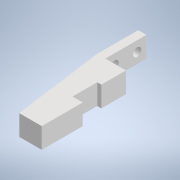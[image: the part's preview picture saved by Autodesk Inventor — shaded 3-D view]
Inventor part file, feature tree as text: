
AUTODESK INVENTOR PART (.ipt)
format: ipt  version: 2021 (Build 250183000, 183)  size: 149,504 bytes
history: native  units: mm
features: move_body x5, direct_edit x4, other x4, extrude x3, sketch x3, reference x2, fillet x1
ambient origin geometry x8: Origin, YZ Plane, XZ Plane, XY Plane, X Axis, Y Axis, Z Axis, Center Point
bodies: Solid1 (feature_tree)
feature tree (22):
  extrude  "Extrusion1"  Depth=20.0mm
  extrude  "Extrusion2"  Depth=12.0mm
  direct_edit  "Direct Edit1"
  direct_edit  "Direct Edit2"
  direct_edit  "Direct Edit3"
  extrude  "Extrusion3"  Depth=12.0mm
  direct_edit  "Direct Edit4"
  fillet  "Fillet1"  Radius=10.0mm
  sketch  "Sketch1"  dims[d0=4.0mm d1=20.0mm]
  sketch  "Sketch2"  dims[d2=14.0mm d3=12.0mm]
  reference  "Reference1"
  reference  "Reference2"
  sketch  "Sketch3"  dims[d4=12.0mm d5=12.0mm d6=10.0mm d7=20.0mm d8=10.0mm d9=0.0mm d10=10.0mm d11=0.0mm d12=0.0mm d13=0.0mm d14=7.0mm d15=0.0mm d16=0.0mm d17=2.0mm d18=0.0mm d19=0.0mm d20=8.0mm d21=0.0mm d22=0.0mm d23=7.75mm d24=10.0mm d25=0.0mm d26=0.0mm d27=0.0mm d28=0.5mm d29=2.0mm]
  parser-record x1  (decoder bookkeeping rows leaked as tree rows — omitted from the tree; the rows remain in map.json)
  other  "whole_assembly.iam"
  other  "539636 HGP-16-A-B-SSK---(asm_0_-ZH):1"
  other  "HGP-16---(116_JAW):2"
  move_body  "Move1"
  move_body  "Move2"
  move_body  "Move3"
  move_body  "Move4"
  move_body  "Move5"
note: 1 file-system path scrubbed to <path> (originals preserved in map.json)
